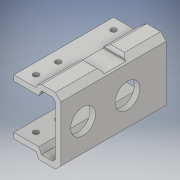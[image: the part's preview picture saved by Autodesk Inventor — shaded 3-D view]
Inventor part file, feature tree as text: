
AUTODESK INVENTOR PART (.ipt)
format: ipt  version: 2018 (Build 220112000, 112)  size: 230,912 bytes
history: native  units: in
note: dims shown in document units (in); Inventor stores cm internally (conversion verified against a paired STEP export)
features: chamfer x6, hole x5, extrude x3, sketch x3
ambient origin geometry x8: Origin, YZ Plane, XZ Plane, XY Plane, X Axis, Y Axis, Z Axis, Center Point
bodies: Body1 (feature_tree)
feature tree (17):
  extrude  "Extrusion2"  Depth=2.0in
  hole  "Hole4"  [1 undecoded]
  hole  "Hole5"  [1 undecoded]
  hole  "Hole6"  [1 undecoded]
  hole  "Hole7"  [1 undecoded]
  hole  "Hole8"  [1 undecoded]
  extrude  "Extrusion3"  Depth=0.25in
  extrude  "Extrusion4"  Depth=1.0in
  chamfer  "Chamfer1"  Distance=0.25in
  chamfer  "Chamfer2"  Distance=0.125in
  chamfer  "Chamfer3"  Distance=0.125in
  chamfer  "Chamfer10"  Distance=0.125in
  chamfer  "Chamfer11"  Distance=0.125in
  chamfer  "Chamfer12"  Distance=0.125in
  sketch  "Sketch1"  dims[d62=1.0in d63=2.0in]
  sketch  "Sketch2"  dims[d64=1.125in d65=0.25in]
  sketch  "Sketch3"  dims[d66=0.25in d67=1.0in d68=0.25in d71=0.125in d72=0.125in d73=0.25in d76=1.0in d77=0.25in d78=0.125in d79=0.125in d80=0.125in d81=0.125in d82=0.125in d83=0.125in d84=4.5in d85=0.0in d86=1.0in d87=1.25in d88=1.125in d89=0.75in d90=0.375in d91=0.25in d92=0.5635in d93=1.0in d94=0.8108in d95=1.25in d96=3.0in d97=1.125in d98=0.75in d99=0.375in d100=0.25in d101=0.5635in d102=1.0in d103=0.8108in d104=0.5in d105=0.5in d106=0.25in d107=0.75in d108=0.375in d109=0.25in d110=0.5635in d111=1.0in d112=0.8108in d113=1.5in d114=0.5in d115=0.25in d116=0.75in d117=0.375in d118=0.25in d119=0.5635in d120=1.0in d121=0.8108in d122=0.5in d123=0.5in d124=0.25in d125=0.75in d126=0.375in d127=0.25in d128=0.5635in d129=1.0in d130=0.8108in d131=0.75in d132=3.0in d133=0.25in d134=0.25in d135=0.0in d136=2.0in d138=3.0in d139=0.0in d140=0.125in d141=0.125in d142=45.0deg d143=0.125in d144=0.125in d145=45.0deg d146=0.125in d147=0.125in d148=45.0deg d167=0.125in d168=0.125in d169=45.0deg d170=0.1875in d171=0.125in d172=0.125in d173=45.0deg d174=0.125in d175=0.125in d176=45.0deg]
note: 5 required parameter values undecoded (feature->parameter linkage not recoverable at this tier; creation-order binding heuristic only, values carry confidence <= 0.55)
